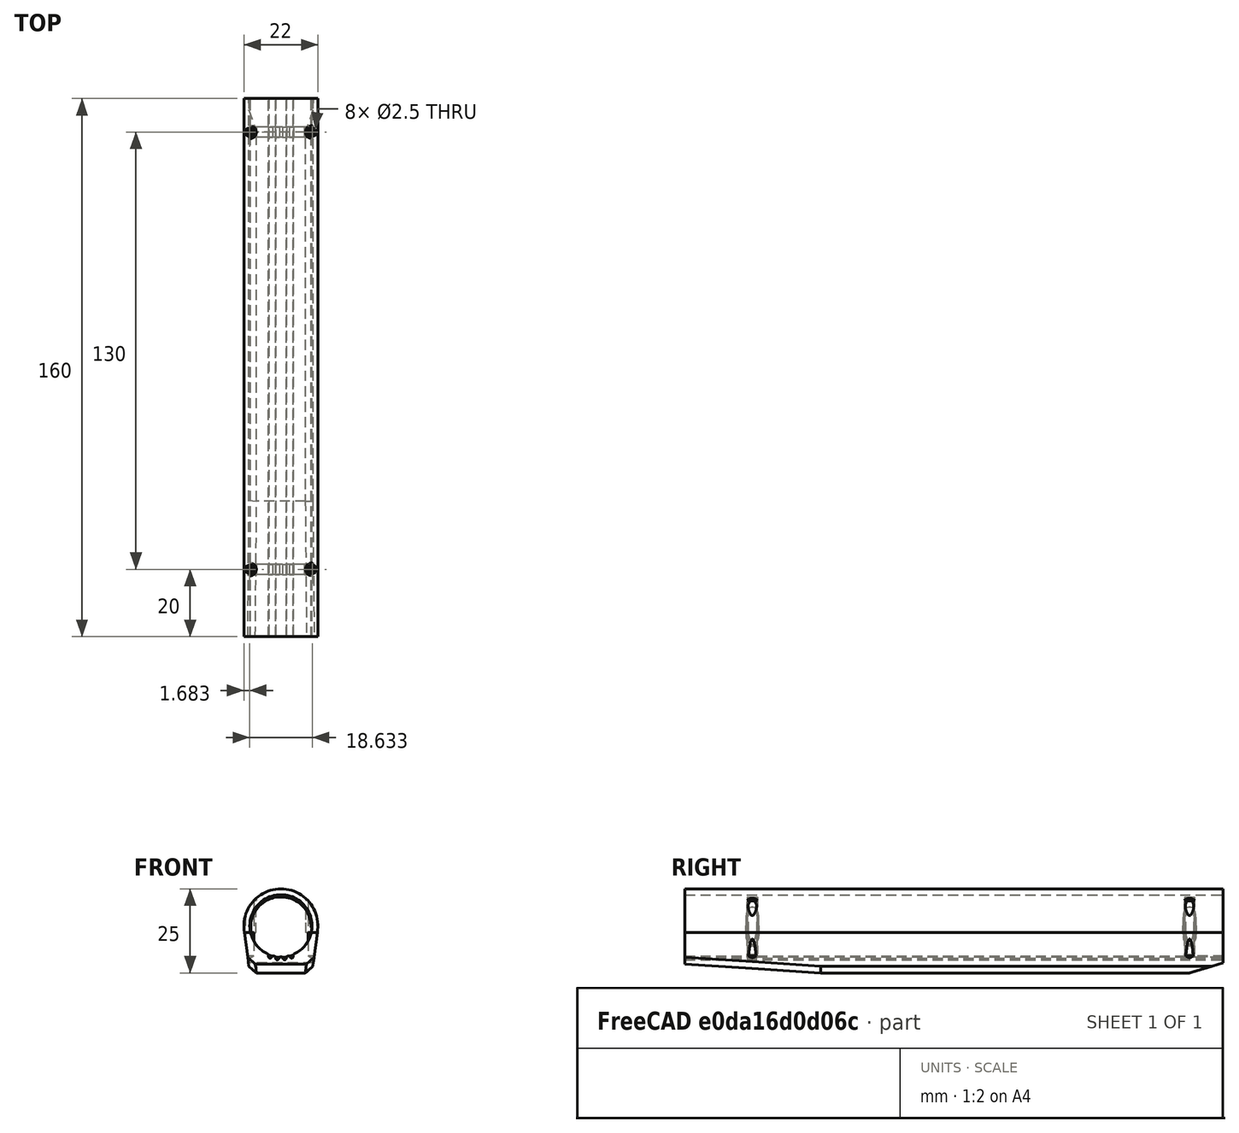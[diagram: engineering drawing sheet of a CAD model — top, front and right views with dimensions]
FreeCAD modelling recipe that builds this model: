
FCSTD DOCUMENT  (FreeCAD 0.20R29177 (Git))
Label: ScrewDriverV3
License: All rights reserved
LicenseURL: http://en.wikipedia.org/wiki/All_rights_reserved
objects: Sketcher::SketchObject×6, PartDesign::Pad×3, PartDesign::Body×3, Part::FeaturePython×3, PartDesign::Pocket×2, PartDesign::Chamfer×2, PartDesign::FeatureBase×2, PartDesign::Fillet×1, PartDesign::Hole×1, Part::Plane×1, App::DocumentObjectGroup×1, PartDesign::LinearPattern×1
note: 34 computed .brp shape members not serialized (recipe doc carries the construction recipe); baked Part::Feature solids carry a one-line shape summary decoded from their .brp

FEATURE [Sketcher::SketchObject] Sketch
  FullyConstrained = true
  MapMode = 5
  Placement = pos=(0,0,0) rot=(1,0,0;1.5708rad)
  Support = -> [XZ_Plane]
  sketch-geometry (12):
    g0: ArcOfCircle CenterX=0 CenterY=14 CenterZ=0 NormalX=0 NormalY=0 NormalZ=1 AngleXU=0 Radius=9.25 StartAngle=5.08282 EndAngle=10.6251
    g1: ArcOfCircle CenterX=0 CenterY=14 CenterZ=0 NormalX=0 NormalY=0 NormalZ=1 AngleXU=0 Radius=11 StartAngle=6.10035 EndAngle=9.60761
    g2: LineSegment StartX=-10.8167 StartY=12 StartZ=0 EndX=-9.25 EndY=0 EndZ=0
    g3: LineSegment StartX=9.25 StartY=0 StartZ=0 EndX=10.8167 EndY=12 EndZ=0
    g4: LineSegment StartX=9.25 StartY=0 StartZ=0 EndX=-9.25 EndY=0 EndZ=0
    g5: ArcOfCircle CenterX=-1.1 CenterY=4.4 CenterZ=0 NormalX=0 NormalY=0 NormalZ=1 AngleXU=0 Radius=0.5 StartAngle=2.04143 EndAngle=7.15518
    g6: ArcOfCircle CenterX=-3.2 CenterY=4.9 CenterZ=0 NormalX=0 NormalY=0 NormalZ=1 AngleXU=0 Radius=0.5 StartAngle=1.8726 EndAngle=6.87589
    g7: ArcOfCircle CenterX=1.1 CenterY=4.4 CenterZ=0 NormalX=0 NormalY=0 NormalZ=1 AngleXU=0 Radius=0.5 StartAngle=2.2696 EndAngle=7.38335
    g8: ArcOfCircle CenterX=3.2 CenterY=4.9 CenterZ=0 NormalX=0 NormalY=0 NormalZ=1 AngleXU=0 Radius=0.5 StartAngle=2.54889 EndAngle=7.55217
    g9: ArcOfCircle CenterX=0 CenterY=14 CenterZ=0 NormalX=0 NormalY=0 NormalZ=1 AngleXU=0 Radius=9.25 StartAngle=4.85632 EndAngle=5.01825
    g10: ArcOfCircle CenterX=0 CenterY=14 CenterZ=0 NormalX=0 NormalY=0 NormalZ=1 AngleXU=0 Radius=9.25 StartAngle=4.62814 EndAngle=4.79663
    g11: ArcOfCircle CenterX=0 CenterY=14 CenterZ=0 NormalX=0 NormalY=0 NormalZ=1 AngleXU=0 Radius=9.25 StartAngle=4.40653 EndAngle=4.56846
  constraints (39):
    c: PointOnObject(g0,g-2)
    c: Diameter(g0) = 18.5
    c: DistanceY(g-1,g0) = 14
    c: Coincident(g1,g0)
    c: Diameter(g1) = 22
    c: PointOnObject(g2,g-1)
    c: PointOnObject(g3,g-1)
    c: Coincident(g4,g3)
    c: Coincident(g4,g2)
    c: DistanceX(g-1,g3) = 9.25
    c: DistanceX(g2,g-1) = 9.25
    c: DistanceY(g-1,g2) = 12
    c: DistanceY(g3,g3) = 12
    c: Coincident(g1,g2)
    c: Coincident(g1,g3)
    c: Equal(g8,g7)
    c: Equal(g7,g5)
    c: Equal(g5,g6)
    c: Symmetric(g5,g7,g-2)
    c: Symmetric(g8,g6,g-2)
    c: DistanceX(g5,g-1) = 1.1
    c: Diameter(g8) = 1
    c: DistanceY(g-1,g5) = 4.4
    c: DistanceY(g-1,g6) = 4.9
    c: DistanceX(g8) = 3.2
    c: Coincident(g8,g0)
    c: Coincident(g8,g9)
    c: Equal(g0,g9)
    c: Coincident(g0,g9)
    c: Coincident(g7,g9)
    c: Coincident(g7,g10)
    c: Equal(g0,g10)
    c: Coincident(g0,g10)
    c: Coincident(g5,g10)
    c: Coincident(g5,g11)
    c: Equal(g0,g11)
    c: Coincident(g0,g11)
    c: Coincident(g6,g11)
    c: Coincident(g6,g0)
FEATURE [PartDesign::Pad] Pad
  Direction = (0,-1,-2e-16)
  Length = 160
  Length2 = 10
  Placement = pos=(0,0,0) rot=(1,0,0;1.5708rad)
  Profile = -> Sketch
  ReferenceAxis = -> Sketch [N_Axis]
  Type = 0
FEATURE [PartDesign::Fillet] Fillet
  Base = -> Pad [Edge14,Edge17,Edge20,Edge23,Edge26,Edge29,Edge32,Edge13]
  BaseFeature = -> Pad
  Placement = pos=(0,0,0) rot=(1,0,0;1.5708rad)
  Radius = 0.5
  SupportTransform = false
  UseAllEdges = false
FEATURE [Sketcher::SketchObject] Sketch004
  FullyConstrained = false
  MapMode = 5
  Support = -> [XY_Plane]
  sketch-geometry (4):
    g0: Circle CenterX=-9.31665 CenterY=-10 CenterZ=0 NormalX=0 NormalY=0 NormalZ=1 AngleXU=0 Radius=1.95
    g1: Circle CenterX=9.31665 CenterY=-10 CenterZ=0 NormalX=0 NormalY=0 NormalZ=1 AngleXU=0 Radius=1.95
    g2: Circle CenterX=-9.31665 CenterY=-140 CenterZ=0 NormalX=0 NormalY=0 NormalZ=1 AngleXU=0 Radius=1.95
    g3: Circle CenterX=9.31665 CenterY=-140 CenterZ=0 NormalX=0 NormalY=0 NormalZ=1 AngleXU=0 Radius=1.95
  constraints (4):
    c: Diameter(g0) = 3.9
    c: Diameter(g1) = 3.9
    c: Equal(g3,g2)
    c: Diameter(g3) = 3.9
FEATURE [PartDesign::Pad] Pad001  label="ScrewHole"
  BaseFeature = -> Fillet
  Direction = (0,0,1)
  Length = 23
  Length2 = 10
  Placement = pos=(0,0,0) rot=(1,0,0;1.5708rad)
  Profile = -> Sketch004
  ReferenceAxis = -> Sketch004 [N_Axis]
  Type = 0
FEATURE [Sketcher::SketchObject] Sketch005
  AttachmentOffset = pos=(0,0,23) rot=(0,0,1;0rad)
  ExternalGeometry = -> [Pad001]
  FullyConstrained = false
  MapMode = 5
  Placement = pos=(0,0,23) rot=(0,0,1;0rad)
  Support = -> [XY_Plane]
  sketch-geometry (4):
    g0: Circle CenterX=-9.31665 CenterY=-10 CenterZ=0 NormalX=0 NormalY=0 NormalZ=1 AngleXU=0 Radius=1.95
    g1: Circle CenterX=-9.31665 CenterY=-140 CenterZ=0 NormalX=0 NormalY=0 NormalZ=1 AngleXU=0 Radius=1.95
    g2: Circle CenterX=9.31665 CenterY=-140 CenterZ=0 NormalX=0 NormalY=0 NormalZ=1 AngleXU=0 Radius=1.95
    g3: Circle CenterX=9.31665 CenterY=-10 CenterZ=0 NormalX=0 NormalY=0 NormalZ=1 AngleXU=0 Radius=1.95
  constraints (5):
    c: Coincident(g0,g-4)
    c: Coincident(g1,g-6)
    c: Coincident(g2,g-5)
    c: Equal(g1,g2)
    c: Coincident(g3,g-3)
FEATURE [PartDesign::Hole] Hole
  BaseFeature = -> Pad001
  CustomThreadClearance = 0
  Depth = 18
  DepthType = 0
  Diameter = 2.5
  DrillForDepth = false
  DrillPoint = 1
  DrillPointAngle = 118
  HoleCutCountersinkAngle = 90
  HoleCutCustomValues = false
  HoleCutDepth = 1.5
  HoleCutDiameter = 4
  HoleCutType = 3
  ModelThread = false
  Placement = pos=(0,0,0) rot=(1,0,0;1.5708rad)
  Profile = -> Sketch005
  Tapered = false
  TaperedAngle = 90
  ThreadClass = 0
  ThreadDepth = 18
  ThreadDepthType = 0
  ThreadDirection = 0
  ThreadFit = 0
  ThreadSize = 9
  ThreadType = 1
  Threaded = true
  UseCustomThreadClearance = false
FEATURE [Sketcher::SketchObject] Sketch006
  ExternalGeometry = -> [Hole]
  FullyConstrained = false
  MapMode = 5
  Placement = pos=(0,0,0) rot=(1,0,0;1.5708rad)
  Support = -> [XZ_Plane]
  sketch-geometry (8):
    g0: LineSegment StartX=-13 StartY=26 StartZ=0 EndX=13 EndY=26 EndZ=0
    g1: LineSegment StartX=13 StartY=26 StartZ=0 EndX=13 EndY=-2 EndZ=0
    g2: LineSegment StartX=13 StartY=-2 StartZ=0 EndX=-13 EndY=-2 EndZ=0
    g3: LineSegment StartX=-13 StartY=-2 StartZ=0 EndX=-13 EndY=26 EndZ=0
    g4: LineSegment StartX=-9.25 StartY=0 StartZ=0 EndX=9.25 EndY=0 EndZ=0
    g5: ArcOfCircle CenterX=0 CenterY=14 CenterZ=0 NormalX=0 NormalY=0 NormalZ=1 AngleXU=0 Radius=11 StartAngle=6.10035 EndAngle=9.60761
    g6: LineSegment StartX=-10.8167 StartY=12 StartZ=0 EndX=-9.25 EndY=0 EndZ=0
    g7: LineSegment StartX=10.8167 StartY=12 StartZ=0 EndX=9.25 EndY=0 EndZ=0
  constraints (20):
    c: Coincident(g0,g1)
    c: Coincident(g1,g2)
    c: Coincident(g2,g3)
    c: Coincident(g3,g0)
    c: Horizontal(g0)
    c: Horizontal(g2)
    c: Vertical(g1)
    c: Vertical(g3)
    c: DistanceY(g1,g1) = 28
    c: Coincident(g5,g-4)
    c: Coincident(g6,g-5)
    c: Coincident(g6,g4)
    c: Coincident(g5,g6)
    c: Coincident(g4,g-5)
    c: Coincident(g4,g-6)
    c: Coincident(g7,g5)
    c: Coincident(g7,g4)
    c: Coincident(g5,g-6)
    c: Distance(g5,g5) = 11
    c: Distance(g5,g5) = 11
FEATURE [PartDesign::Pocket] Pocket
  BaseFeature = -> Hole
  Direction = (0,1,2e-16)
  Length = 164
  Length2 = 5
  Placement = pos=(0,0,0) rot=(1,0,0;1.5708rad)
  Profile = -> Sketch006
  ReferenceAxis = -> Sketch006 [N_Axis]
  Reversed = true
  Type = 0
FEATURE [Sketcher::SketchObject] Sketch007
  FullyConstrained = false
  MapMode = 5
  Placement = pos=(0,0,0) rot=(0.57735,0.57735,0.57735;2.0944rad)
  Support = -> [YZ_Plane]
  sketch-geometry (3):
    g0: LineSegment StartX=-163.142 StartY=2.84826 StartZ=0 EndX=-107.866 EndY=-0.772404 EndZ=0
    g1: LineSegment StartX=-163.142 StartY=2.84826 StartZ=0 EndX=-163.142 EndY=-0.772404 EndZ=0
    g2: LineSegment StartX=-163.142 StartY=-0.772404 StartZ=0 EndX=-107.866 EndY=-0.772404 EndZ=0
  constraints (5):
    c: Coincident(g1,g0)
    c: Vertical(g1)
    c: Coincident(g2,g1)
    c: Coincident(g2,g0)
    c: Horizontal(g2)
FEATURE [PartDesign::Pocket] Pocket001
  BaseFeature = -> Pocket
  Direction = (-1,2e-16,-3e-16)
  Length = 20
  Length2 = 5
  Midplane = true
  Placement = pos=(0,0,0) rot=(1,0,0;1.5708rad)
  Profile = -> Sketch007
  ReferenceAxis = -> Sketch007 [N_Axis]
  Type = 0
FEATURE [PartDesign::Chamfer] Chamfer
  Angle = 45
  Base = -> Pocket001 [Edge111,Edge110]
  BaseFeature = -> Pocket001
  ChamferType = 1
  FlipDirection = false
  Placement = pos=(0,0,0) rot=(1,0,0;1.5708rad)
  Size = 2
  Size2 = 2
  SupportTransform = false
  UseAllEdges = false
FEATURE [PartDesign::Chamfer] Chamfer001
  Angle = 45
  Base = -> Chamfer [Edge4]
  BaseFeature = -> Chamfer
  ChamferType = 1
  FlipDirection = false
  Placement = pos=(0,0,0) rot=(1,0,0;1.5708rad)
  Size = 3
  Size2 = 10
  SupportTransform = false
  UseAllEdges = false
FEATURE [PartDesign::Body] Body
  Group = -> [Sketch,Pad,Fillet,Sketch004,Pad001,Sketch005,Hole,Sketch006,Pocket,Sketch007,Pocket001,Chamfer,Chamfer001]
  Origin = -> Origin
  Tip = -> Chamfer001
FEATURE [Part::Plane] Plane
  AttacherType = Attacher::AttachEngine3D
  Length = 170
  Placement = pos=(-24,2,12) rot=(0,0,1;4.71239rad)
  Width = 50
FEATURE [Part::FeaturePython] Slice  # WARN: FeaturePython — macro-defined, semantics opaque (R4)
  Base = -> Body
  Mode = 1
  Tolerance = 0
  Tools = -> [Plane]
FEATURE [Part::FeaturePython] Slice_child0  label="Slice.0"  # WARN: FeaturePython — macro-defined, semantics opaque (R4)
  Base = -> Slice
  FilterType = 1
  Invert = false
  OverrideMaxVal = 0
  Placement = pos=(-23,0,24) rot=(0,1,0;3.14159rad)
  WindowFrom = 80
  WindowTo = 100
  items = 0
FEATURE [Part::FeaturePython] Slice_child1  label="Slice.1"  # WARN: FeaturePython — macro-defined, semantics opaque (R4)
  Base = -> Slice
  FilterType = 1
  Invert = false
  OverrideMaxVal = 0
  WindowFrom = 80
  WindowTo = 100
  items = 1
FEATURE [App::DocumentObjectGroup] GrExplode_Slice  label="Exploded Slice"
  Group = -> [Slice_child1,Slice_child0]
FEATURE [PartDesign::FeatureBase] BaseFeature  label="BottomBase"
  BaseFeature = -> Slice_child1
FEATURE [PartDesign::FeatureBase] BaseFeature001  label="TopBase"
  BaseFeature = -> Slice_child0
FEATURE [PartDesign::Body] Body001  label="Top"
  BaseFeature = -> Slice_child0
  Group = -> [BaseFeature001]
  Origin = -> Origin001
  Tip = -> BaseFeature001
FEATURE [Sketcher::SketchObject] Sketch008
  AttachmentOffset = pos=(0,0,8.5) rot=(0,0,1;0rad)
  FullyConstrained = true
  MapMode = 5
  Placement = pos=(0,-8.5,1.9e-15) rot=(1,0,0;1.5708rad)
  Support = -> [XZ_Plane002]
  sketch-geometry (1):
    g0: Circle CenterX=0 CenterY=13.6 CenterZ=0 NormalX=0 NormalY=0 NormalZ=1 AngleXU=0 Radius=9
  constraints (3):
    c: Diameter(g0) = 18
    c: DistanceY(g-1,g0) = 13.6
    c: PointOnObject(g0,g-2)
FEATURE [PartDesign::Pad] Pad002
  BaseFeature = -> BaseFeature
  Direction = (0,-1,2e-16)
  Length = 3
  Length2 = 10
  Profile = -> Sketch008
  ReferenceAxis = -> Sketch008 [N_Axis]
  Type = 0
FEATURE [PartDesign::LinearPattern] LinearPattern
  BaseFeature = -> Pad002
  Direction = -> Y_Axis002
  Length = 130
  Occurrences = 2
  Originals = -> [Pad002]
  Reversed = true
FEATURE [PartDesign::Body] Body002  label="Bottom"
  BaseFeature = -> Slice_child1
  Group = -> [BaseFeature,Sketch008,Pad002,LinearPattern]
  Origin = -> Origin002
  Tip = -> LinearPattern
